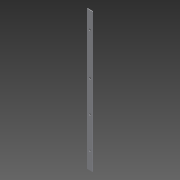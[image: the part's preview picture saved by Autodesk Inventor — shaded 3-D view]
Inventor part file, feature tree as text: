
AUTODESK INVENTOR PART (.ipt)
format: ipt  version: 2015 (Build 190159000, 159)  size: 96,256 bytes
history: native  units: mm
features: sketch x2, other x1, extrude x1, hole x1
ambient origin geometry x8: Origin, YZ Plane, XZ Plane, XY Plane, X Axis, Y Axis, Z Axis, Center Point
bodies: Body1 (feature_tree)
feature tree (5):
  other  "Bryła1"
  extrude  "Wyciągnięcie proste1"  Depth=15.9mm
  hole  "Otwór1"  [1 undecoded]
  sketch  "Szkic1"
  sketch  "Szkic2"
note: 1 required parameter value undecoded (feature->parameter linkage not recoverable at this tier; creation-order binding heuristic only, values carry confidence <= 0.55)
